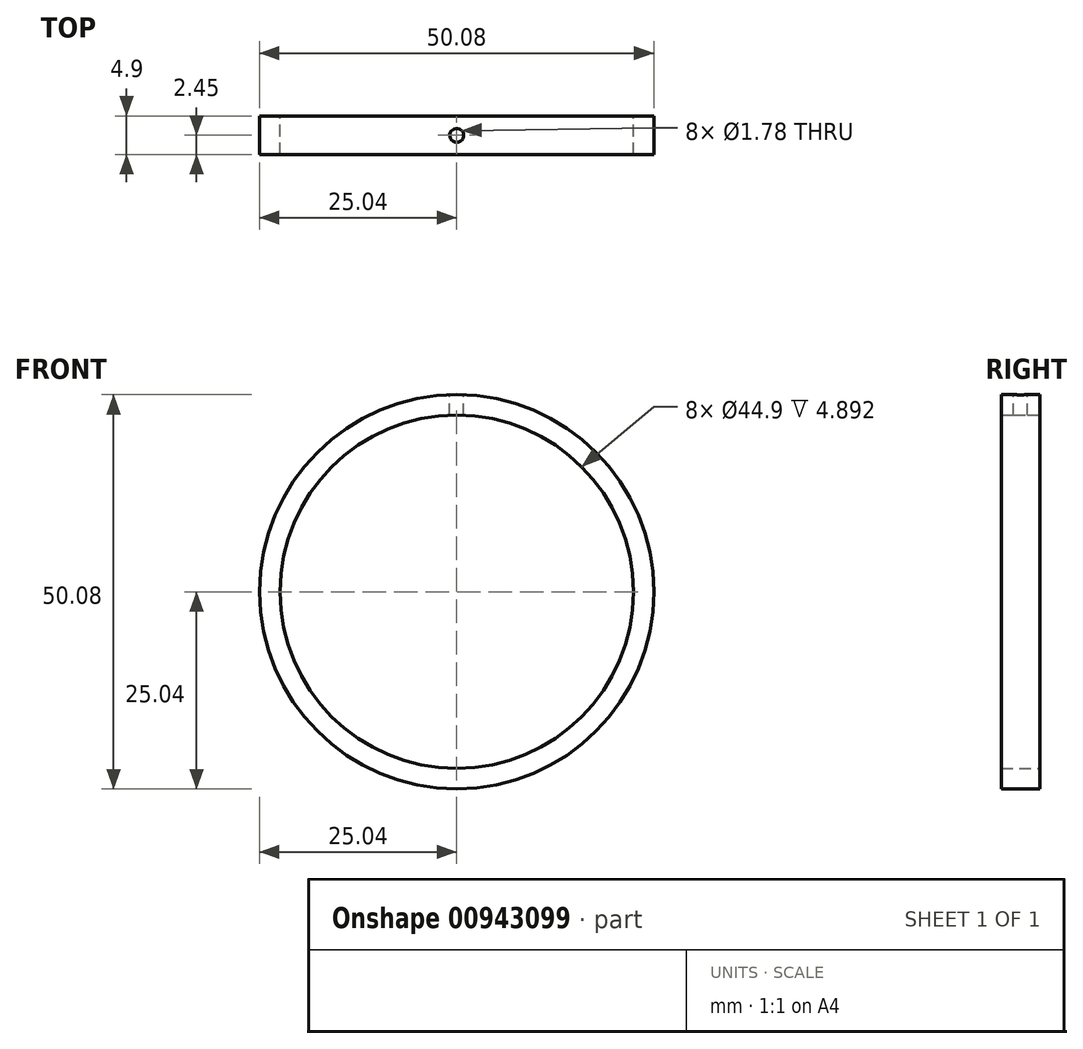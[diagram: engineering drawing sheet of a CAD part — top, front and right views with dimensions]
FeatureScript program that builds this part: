
annotation { "Feature Type Name" : "Feature", "Feature Type Description" : "" }
export const myFeature = defineFeature(function(context is Context, id is Id, definition is map)
    precondition{}
    {
        {
            var Q0;
            Q0=qCreatedBy(makeId("Front.planeOp"),FACE);
            var sketch = newSketch(context, id + "F0", { "sketchPlane" : qUnion([Q0])});
            skCircle(sketch, "E0", {"center": v(0, 0) * mm, "radius": 25.04 * mm});
            skCircle(sketch, "E1.0", {"center": v(0, 0) * mm, "radius": 22.45 * mm});
            skPoint(sketch, "E2", {"position": v(0, 25.04) * mm});
            skSolve(sketch);
        }
        {
            var Q0;
            Q0=makeQuery(id+"F0.imprint","IMPRINT",FACE,{"disambiguationData":[TD([[makeQuery(id+"F0.imprint","IMPRINT",EDGE,{"derivedFrom":sQuery(id+"F0.wireOp",EDGE,"E0")}),1.0]])]});
            extrude(context, id + "F1", {"entities" : qUnion([Q0]), "endBound" : BoundingType.SYMMETRIC, "depth" : 4.9 * mm, "offsetDistance" : 25.4 * mm});
        }
        {
            var Q0;
            Q0=qCreatedBy(makeId("Top.planeOp"),FACE);
            var Q1;
            Q1=sQuery(id+"F0.wireOp",VERTEX,"E2");
            cPlane(context, id + "F2", {"entities" : qUnion([Q0, Q1]), "cplaneType" : CPlaneType.PLANE_POINT, "offset" : 25.4 * mm, "width" : 152.4 * mm, "height" : 152.4 * mm});
        }
        {
            var Q0;
            Q0=qCreatedBy(id+"F2.planeOp",FACE);
            var sketch = newSketch(context, id + "F3", { "sketchPlane" : qUnion([Q0])});
            skPoint(sketch, "E3", {"position": v(0, 0) * mm});
            skSolve(sketch);
        }
        {
            var Q0;
            Q0=sQuery(id+"F3.wireOp",VERTEX,"E3");
            var Q1;
            Q1=makeQuery(id+"F1.opExtrude","SWEPT_BODY",BODY,{"disambiguationData":[OSD([sQuery(id+"F0.wireOp",EDGE,"E0"),sQuery(id+"F0.wireOp",EDGE,"E1.0")])]});
            hole(context, id + "F4", {"style" : HoleStyle.SIMPLE, "endStyle" : HoleEndStyle.BLIND, "standardTappedOrClearance" : lookupTablePath({ "standard" : "ANSI", "engagement" : "75%", "pitch" : "56 tpi", "size" : "#2", "type" : "Tapped" }), "standardBlindInLast" : lookupTablePath({ "standard" : "ANSI", "fit" : "Normal", "engagement" : "75%", "pitch" : "56 tpi", "size" : "#2", "type" : "Clearance & tapped" }), "holeDiameter" : 1.78 * mm, "majorDiameter" : 2.18 * mm, "showTappedDepth" : true, "holeDepth" : 14.06 * mm, "isTappedThrough" : true, "tappedDepth" : 12.7 * mm, "tapClearance" : 3, "locations" : qUnion([Q0]), "scope" : qUnion([Q1])});
        }
    });
